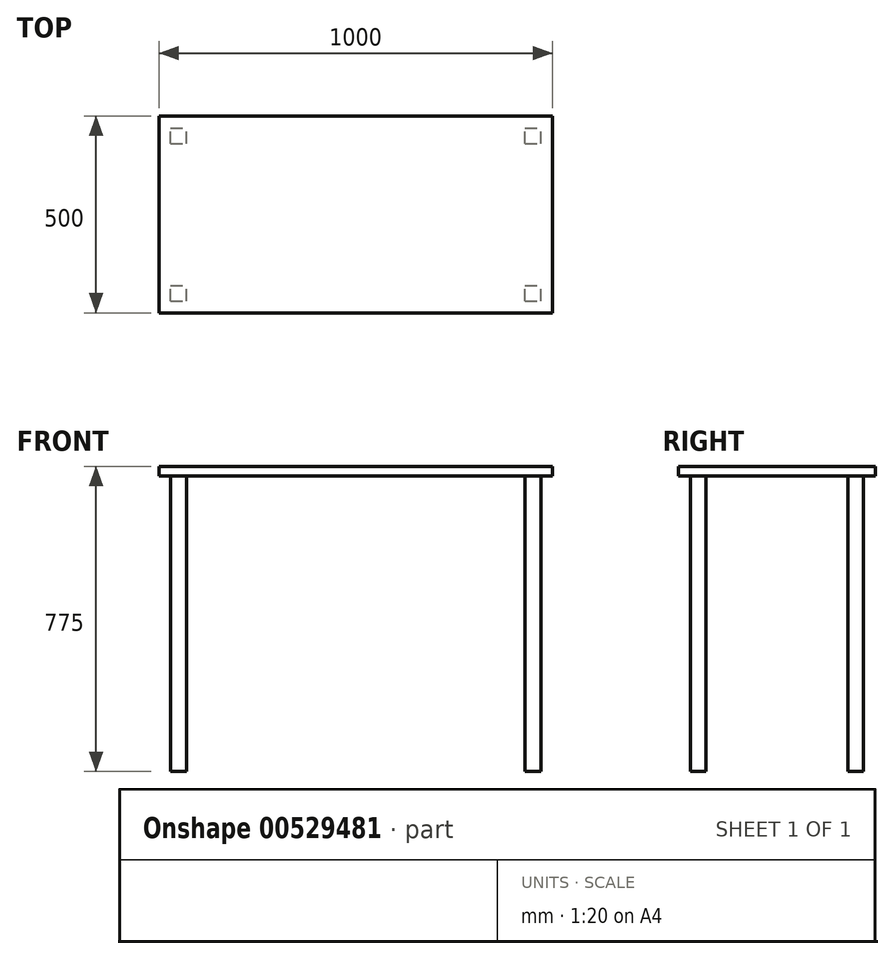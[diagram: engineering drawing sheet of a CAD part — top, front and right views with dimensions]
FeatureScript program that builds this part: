
annotation { "Feature Type Name" : "Feature", "Feature Type Description" : "" }
export const myFeature = defineFeature(function(context is Context, id is Id, definition is map)
    precondition{}
    {
        {
            var Q0;
            Q0=qCreatedBy(makeId("Top.planeOp"),FACE);
            var sketch = newSketch(context, id + "F0", { "sketchPlane" : qUnion([Q0])});
            skLineSegment(sketch, "E0.bottom", {"start": v(0, 0) * mm, "end": v(1000, 0) * mm});
            skLineSegment(sketch, "E0.top", {"start": v(0, 500) * mm, "end": v(1000, 500) * mm});
            skLineSegment(sketch, "E0.left", {"start": v(0, 0) * mm, "end": v(0, 500) * mm});
            skLineSegment(sketch, "E0.right", {"start": v(1000, 0) * mm, "end": v(1000, 500) * mm});
            skSolve(sketch);
        }
        {
            var Q0;
            Q0=makeQuery(id+"F0.imprint","IMPRINT",FACE,{"disambiguationData":[TD([[makeQuery(id+"F0.imprint","IMPRINT",EDGE,{"derivedFrom":sQuery(id+"F0.wireOp",EDGE,"E0.bottom")}),1.0]])]});
            extrude(context, id + "F1", {"entities" : qUnion([Q0]), "depth" : 25 * mm, "offsetDistance" : 25 * mm});
        }
        {
            var Q0;
            Q0=makeQuery(id+"F1.opExtrude","CAP_FACE",FACE,{"disambiguationData":[OSD([sQuery(id+"F0.wireOp",EDGE,"E0.bottom"),sQuery(id+"F0.wireOp",EDGE,"E0.top"),sQuery(id+"F0.wireOp",EDGE,"E0.left"),sQuery(id+"F0.wireOp",EDGE,"E0.right")])],"isStart":true});
            var sketch = newSketch(context, id + "F2", { "sketchPlane" : qUnion([Q0])});
            skLineSegment(sketch, "E1.bottom", {"start": v(30, -30) * mm, "end": v(70, -30) * mm});
            skLineSegment(sketch, "E1.top", {"start": v(30, -70) * mm, "end": v(70, -70) * mm});
            skLineSegment(sketch, "E1.left", {"start": v(30, -30) * mm, "end": v(30, -70) * mm});
            skLineSegment(sketch, "E1.right", {"start": v(70, -30) * mm, "end": v(70, -70) * mm});
            skLineSegment(sketch, "E2.0.1.0", {"start": v(30, -430) * mm, "end": v(70, -430) * mm});
            skLineSegment(sketch, "E2.0.1.1", {"start": v(30, -470) * mm, "end": v(70, -470) * mm});
            skLineSegment(sketch, "E2.0.1.2", {"start": v(30, -430) * mm, "end": v(30, -470) * mm});
            skLineSegment(sketch, "E2.0.1.3", {"start": v(70, -430) * mm, "end": v(70, -470) * mm});
            skLineSegment(sketch, "E2.1.0.0", {"start": v(930, -30) * mm, "end": v(970, -30) * mm});
            skLineSegment(sketch, "E2.1.0.1", {"start": v(930, -70) * mm, "end": v(970, -70) * mm});
            skLineSegment(sketch, "E2.1.0.2", {"start": v(930, -30) * mm, "end": v(930, -70) * mm});
            skLineSegment(sketch, "E2.1.0.3", {"start": v(970, -30) * mm, "end": v(970, -70) * mm});
            skLineSegment(sketch, "E2.1.1.0", {"start": v(930, -430) * mm, "end": v(970, -430) * mm});
            skLineSegment(sketch, "E2.1.1.1", {"start": v(930, -470) * mm, "end": v(970, -470) * mm});
            skLineSegment(sketch, "E2.1.1.2", {"start": v(930, -430) * mm, "end": v(930, -470) * mm});
            skLineSegment(sketch, "E2.1.1.3", {"start": v(970, -430) * mm, "end": v(970, -470) * mm});
            skLineSegment(sketch, "E2.direction1", {"start": v(30, -30) * mm, "end": v(940, -30) * mm, "construction": true});
            skLineSegment(sketch, "E2.direction2", {"start": v(30, -30) * mm, "end": v(30, -480) * mm, "construction": true});
            skSolve(sketch);
        }
        {
            var Q0;
            Q0=makeQuery(id+"F2.imprint","IMPRINT",FACE,{"disambiguationData":[TD([[makeQuery(id+"F2.imprint","IMPRINT",EDGE,{"derivedFrom":sQuery(id+"F2.wireOp",EDGE,"E1.bottom")}),-1.0]])]});
            var Q1;
            Q1=makeQuery(id+"F2.imprint","IMPRINT",FACE,{"disambiguationData":[TD([[makeQuery(id+"F2.imprint","IMPRINT",EDGE,{"derivedFrom":sQuery(id+"F2.wireOp",EDGE,"E2.0.1.0")}),-1.0]])]});
            var Q2;
            Q2=makeQuery(id+"F2.imprint","IMPRINT",FACE,{"disambiguationData":[TD([[makeQuery(id+"F2.imprint","IMPRINT",EDGE,{"derivedFrom":sQuery(id+"F2.wireOp",EDGE,"E2.1.0.0")}),-1.0]])]});
            var Q3;
            Q3=makeQuery(id+"F2.imprint","IMPRINT",FACE,{"disambiguationData":[TD([[makeQuery(id+"F2.imprint","IMPRINT",EDGE,{"derivedFrom":sQuery(id+"F2.wireOp",EDGE,"E2.1.1.0")}),-1.0]])]});
            extrude(context, id + "F3", {"entities" : qUnion([Q0, Q1, Q2, Q3]), "operationType" : NewBodyOperationType.ADD, "depth" : 750 * mm, "offsetDistance" : 25 * mm});
        }
    });
